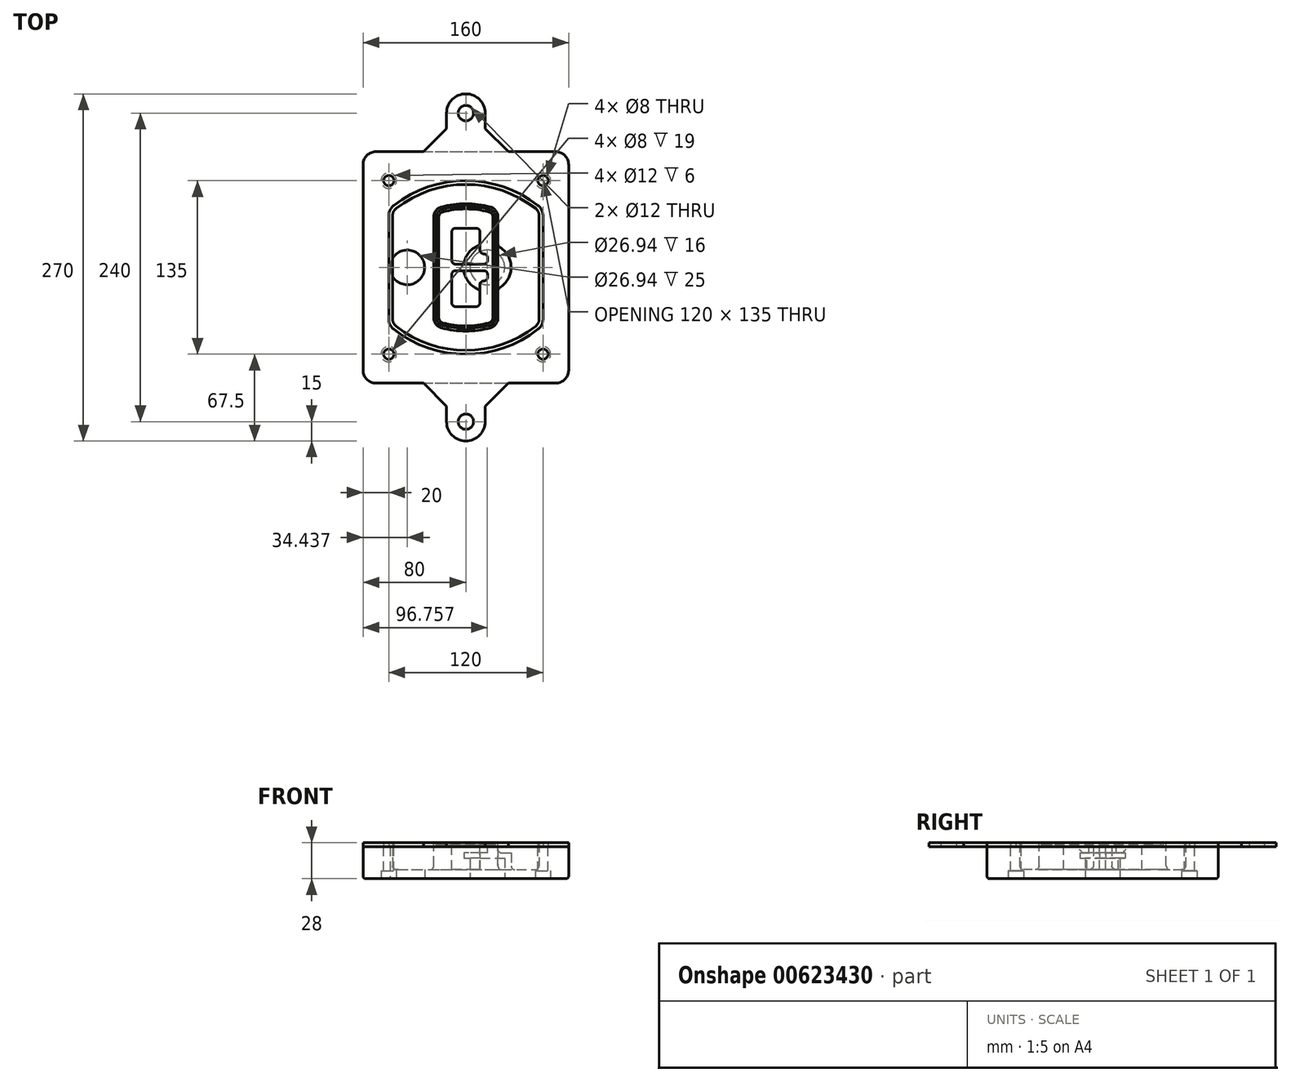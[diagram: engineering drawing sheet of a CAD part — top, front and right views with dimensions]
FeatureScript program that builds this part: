
annotation { "Feature Type Name" : "Feature", "Feature Type Description" : "" }
export const myFeature = defineFeature(function(context is Context, id is Id, definition is map)
    precondition{}
    {
        {
            var Q0;
            Q0=qCreatedBy(makeId("Top.planeOp"),FACE);
            var sketch = newSketch(context, id + "F0", { "sketchPlane" : qUnion([Q0])});
            skPoint(sketch, "E0.rect.middle", {"position": v(0, 0) * mm});
            skLineSegment(sketch, "E1.bottom", {"start": v(-70, -90) * mm, "end": v(70, -90) * mm});
            skLineSegment(sketch, "E1.top", {"start": v(-70, 90) * mm, "end": v(70, 90) * mm});
            skLineSegment(sketch, "E1.left", {"start": v(-80, -80) * mm, "end": v(-80, 80) * mm});
            skLineSegment(sketch, "E1.right", {"start": v(80, -80) * mm, "end": v(80, 80) * mm});
            skLineSegment(sketch, "E2", {"start": v(-80, 90) * mm, "end": v(80, -90) * mm, "construction": true});
            skLineSegment(sketch, "E3", {"start": v(80, 90) * mm, "end": v(-80, -90) * mm, "construction": true});
            skCircle(sketch, "E4", {"center": v(-60, 67.5) * mm, "radius": 4 * mm});
            skCircle(sketch, "E5", {"center": v(60, 67.5) * mm, "radius": 4 * mm});
            skCircle(sketch, "E6", {"center": v(60, -67.5) * mm, "radius": 4 * mm});
            skCircle(sketch, "E7", {"center": v(-60, -67.5) * mm, "radius": 4 * mm});
            skLineSegment(sketch, "E8", {"start": v(-60, 67.5) * mm, "end": v(60, 67.5) * mm, "construction": true});
            skLineSegment(sketch, "E9", {"start": v(60, 67.5) * mm, "end": v(60, -67.5) * mm, "construction": true});
            skLineSegment(sketch, "E10", {"start": v(60, -67.5) * mm, "end": v(-60, -67.5) * mm, "construction": true});
            skLineSegment(sketch, "E11", {"start": v(-60, -67.5) * mm, "end": v(-60, 67.5) * mm, "construction": true});
            skLineSegment(sketch, "E12", {"start": v(-60, 40.3) * mm, "end": v(-60, -40.3) * mm});
            skLineSegment(sketch, "E13", {"start": v(60, 40.3) * mm, "end": v(60, -40.3) * mm});
            skArc(sketch, "E14", {"start": v(56.15, 48.18) * mm, "mid": v(0, 67.5) * mm, "end": v(-56.15, 48.18) * mm});
            skArc(sketch, "E15", {"start": v(-56.15, -48.18) * mm, "mid": v(0, -67.5) * mm, "end": v(56.15, -48.18) * mm});
            skLineSegment(sketch, "E16", {"start": v(-60, 0) * mm, "end": v(60, 0) * mm, "construction": true});
            skPoint(sketch, "E17.visualSharp", {"position": v(-60, -45) * mm});
            skArc(sketch, "E17.filletArc", {"start": v(-60, -40.3) * mm, "mid": v(-58.99, -44.68) * mm, "end": v(-56.15, -48.18) * mm});
            skPoint(sketch, "E18.visualSharp", {"position": v(-60, 45) * mm});
            skArc(sketch, "E18.filletArc", {"start": v(-56.15, 48.18) * mm, "mid": v(-58.99, 44.68) * mm, "end": v(-60, 40.3) * mm});
            skPoint(sketch, "E19.visualSharp", {"position": v(60, 45) * mm});
            skArc(sketch, "E19.filletArc", {"start": v(60, 40.3) * mm, "mid": v(58.99, 44.68) * mm, "end": v(56.15, 48.18) * mm});
            skPoint(sketch, "E20.visualSharp", {"position": v(60, -45) * mm});
            skArc(sketch, "E20.filletArc", {"start": v(56.15, -48.18) * mm, "mid": v(58.99, -44.68) * mm, "end": v(60, -40.3) * mm});
            skPoint(sketch, "E21.visualSharp", {"position": v(-80, 90) * mm});
            skArc(sketch, "E21.filletArc", {"start": v(-70, 90) * mm, "mid": v(-77.07, 87.07) * mm, "end": v(-80, 80) * mm});
            skPoint(sketch, "E22.visualSharp", {"position": v(80, 90) * mm});
            skArc(sketch, "E22.filletArc", {"start": v(80, 80) * mm, "mid": v(77.07, 87.07) * mm, "end": v(70, 90) * mm});
            skPoint(sketch, "E23.visualSharp", {"position": v(80, -90) * mm});
            skArc(sketch, "E23.filletArc", {"start": v(70, -90) * mm, "mid": v(77.07, -87.07) * mm, "end": v(80, -80) * mm});
            skPoint(sketch, "E24.visualSharp", {"position": v(-80, -90) * mm});
            skArc(sketch, "E24.filletArc", {"start": v(-80, -80) * mm, "mid": v(-77.07, -87.07) * mm, "end": v(-70, -90) * mm});
            skArc(sketch, "E25.0", {"start": v(57, 40.3) * mm, "mid": v(56.3, 43.36) * mm, "end": v(54.3, 45.81) * mm});
            skLineSegment(sketch, "E25.1", {"start": v(57, 40.3) * mm, "end": v(57, -40.3) * mm});
            skArc(sketch, "E25.2", {"start": v(54.3, -45.81) * mm, "mid": v(56.3, -43.36) * mm, "end": v(57, -40.3) * mm});
            skArc(sketch, "E25.3", {"start": v(-54.3, -45.81) * mm, "mid": v(0, -64.5) * mm, "end": v(54.3, -45.81) * mm});
            skArc(sketch, "E25.4", {"start": v(-57, -40.3) * mm, "mid": v(-56.3, -43.36) * mm, "end": v(-54.3, -45.81) * mm});
            skArc(sketch, "E25.5", {"start": v(54.3, 45.81) * mm, "mid": v(0, 64.5) * mm, "end": v(-54.3, 45.81) * mm});
            skLineSegment(sketch, "E25.6", {"start": v(-57, 40.3) * mm, "end": v(-57, -40.3) * mm});
            skArc(sketch, "E25.7", {"start": v(-54.3, 45.81) * mm, "mid": v(-56.3, 43.36) * mm, "end": v(-57, 40.3) * mm});
            skArc(sketch, "E26.0", {"start": v(-58.62, 51.33) * mm, "mid": v(-62.58, 46.43) * mm, "end": v(-64, 40.3) * mm});
            skArc(sketch, "E26.1", {"start": v(58.62, 51.33) * mm, "mid": v(0, 71.5) * mm, "end": v(-58.62, 51.33) * mm});
            skArc(sketch, "E26.2", {"start": v(64, 40.3) * mm, "mid": v(62.58, 46.43) * mm, "end": v(58.62, 51.33) * mm});
            skLineSegment(sketch, "E26.3", {"start": v(64, 40.3) * mm, "end": v(64, -40.3) * mm});
            skArc(sketch, "E26.4", {"start": v(58.62, -51.33) * mm, "mid": v(62.58, -46.43) * mm, "end": v(64, -40.3) * mm});
            skLineSegment(sketch, "E26.5", {"start": v(-64, 40.3) * mm, "end": v(-64, -40.3) * mm});
            skArc(sketch, "E26.6", {"start": v(-58.62, -51.33) * mm, "mid": v(0, -71.5) * mm, "end": v(58.62, -51.33) * mm});
            skArc(sketch, "E26.7", {"start": v(-64, -40.3) * mm, "mid": v(-62.58, -46.43) * mm, "end": v(-58.62, -51.33) * mm});
            skSolve(sketch);
        }
        {
            var Q0;
            Q0=makeQuery(id+"F0.imprint","IMPRINT",FACE,{"disambiguationData":[TD([[makeQuery(id+"F0.imprint","IMPRINT",EDGE,{"derivedFrom":sQuery(id+"F0.wireOp",EDGE,"E1.bottom")}),1.0]])]});
            var Q1;
            Q1=makeQuery(id+"F0.imprint","IMPRINT",FACE,{"disambiguationData":[TD([[makeQuery(id+"F0.imprint","IMPRINT",EDGE,{"derivedFrom":sQuery(id+"F0.wireOp",EDGE,"E12")}),1.0]])]});
            var Q2;
            Q2=makeQuery(id+"F0.imprint","IMPRINT",FACE,{"disambiguationData":[TD([[makeQuery(id+"F0.imprint","IMPRINT",EDGE,{"derivedFrom":sQuery(id+"F0.wireOp",EDGE,"E25.0")}),1.0]])]});
            var Q3;
            Q3=makeQuery(id+"F0.imprint","IMPRINT",FACE,{"disambiguationData":[TD([[makeQuery(id+"F0.imprint","IMPRINT",EDGE,{"derivedFrom":sQuery(id+"F0.wireOp",EDGE,"E12")}),-1.0]])]});
            extrude(context, id + "F1", {"entities" : qUnion([Q0, Q1, Q2, Q3]), "oppositeDirection" : true, "depth" : 25 * mm});
        }
        {
            var Q0;
            Q0=makeQuery(id+"F0.imprint","IMPRINT",FACE,{"disambiguationData":[TD([[makeQuery(id+"F0.imprint","IMPRINT",EDGE,{"derivedFrom":sQuery(id+"F0.wireOp",EDGE,"E12")}),1.0]])]});
            extrude(context, id + "F2", {"entities" : qUnion([Q0]), "operationType" : NewBodyOperationType.ADD, "depth" : 3 * mm});
        }
        {
            var Q0;
            Q0=makeQuery(id+"F0.imprint","IMPRINT",FACE,{"disambiguationData":[TD([[makeQuery(id+"F0.imprint","IMPRINT",EDGE,{"derivedFrom":sQuery(id+"F0.wireOp",EDGE,"E25.0")}),1.0]])]});
            extrude(context, id + "F3", {"entities" : qUnion([Q0]), "operationType" : NewBodyOperationType.REMOVE, "oppositeDirection" : true, "depth" : 18 * mm});
        }
        {
            var Q0;
            Q0=makeQuery(id+"F2.opExtrude","CAP_FACE",FACE,{"disambiguationData":[OSD([sQuery(id+"F0.wireOp",EDGE,"E12"),sQuery(id+"F0.wireOp",EDGE,"E13"),sQuery(id+"F0.wireOp",EDGE,"E14"),sQuery(id+"F0.wireOp",EDGE,"E15"),sQuery(id+"F0.wireOp",EDGE,"E17.filletArc"),sQuery(id+"F0.wireOp",EDGE,"E18.filletArc"),sQuery(id+"F0.wireOp",EDGE,"E19.filletArc"),sQuery(id+"F0.wireOp",EDGE,"E20.filletArc"),sQuery(id+"F0.wireOp",EDGE,"E25.0"),sQuery(id+"F0.wireOp",EDGE,"E25.1"),sQuery(id+"F0.wireOp",EDGE,"E25.2"),sQuery(id+"F0.wireOp",EDGE,"E25.3"),sQuery(id+"F0.wireOp",EDGE,"E25.4"),sQuery(id+"F0.wireOp",EDGE,"E25.5"),sQuery(id+"F0.wireOp",EDGE,"E25.6"),sQuery(id+"F0.wireOp",EDGE,"E25.7")])],"isStart":false});
            var sketch = newSketch(context, id + "F4", { "sketchPlane" : qUnion([Q0])});
            skArc(sketch, "E27.0", {"start": v(-19.08, -46.97) * mm, "mid": v(0, -49.5) * mm, "end": v(19.08, -46.97) * mm});
            skArc(sketch, "E28.0", {"start": v(19.08, 46.97) * mm, "mid": v(0, 49.5) * mm, "end": v(-19.08, 46.97) * mm});
            skLineSegment(sketch, "E29", {"start": v(-25, 39.25) * mm, "end": v(-25, -39.25) * mm});
            skLineSegment(sketch, "E30", {"start": v(25, 39.25) * mm, "end": v(25, -39.25) * mm});
            skLineSegment(sketch, "E31", {"start": v(-25, 45.1) * mm, "end": v(25, 45.1) * mm, "construction": true});
            skLineSegment(sketch, "E32", {"start": v(-25, -45.1) * mm, "end": v(25, -45.1) * mm, "construction": true});
            skPoint(sketch, "E33.visualSharp", {"position": v(-25, 45.1) * mm});
            skArc(sketch, "E33.filletArc", {"start": v(-19.08, 46.97) * mm, "mid": v(-23.35, 44.11) * mm, "end": v(-25, 39.25) * mm});
            skPoint(sketch, "E34.visualSharp", {"position": v(25, 45.1) * mm});
            skArc(sketch, "E34.filletArc", {"start": v(25, 39.25) * mm, "mid": v(23.35, 44.11) * mm, "end": v(19.08, 46.97) * mm});
            skPoint(sketch, "E35.visualSharp", {"position": v(25, -45.1) * mm});
            skArc(sketch, "E35.filletArc", {"start": v(19.08, -46.97) * mm, "mid": v(23.35, -44.11) * mm, "end": v(25, -39.25) * mm});
            skPoint(sketch, "E36.visualSharp", {"position": v(-25, -45.1) * mm});
            skArc(sketch, "E36.filletArc", {"start": v(-25, -39.25) * mm, "mid": v(-23.35, -44.11) * mm, "end": v(-19.08, -46.97) * mm});
            skArc(sketch, "E37.0", {"start": v(54.3, 45.81) * mm, "mid": v(0, 64.5) * mm, "end": v(-54.3, 45.81) * mm});
            skArc(sketch, "E37.1", {"start": v(-54.3, 45.81) * mm, "mid": v(-56.3, 43.36) * mm, "end": v(-57, 40.3) * mm});
            skLineSegment(sketch, "E37.2", {"start": v(-57, 40.3) * mm, "end": v(-57, -40.3) * mm});
            skArc(sketch, "E37.3", {"start": v(-57, -40.3) * mm, "mid": v(-56.3, -43.36) * mm, "end": v(-54.3, -45.81) * mm});
            skArc(sketch, "E37.4", {"start": v(-54.3, -45.81) * mm, "mid": v(0, -64.5) * mm, "end": v(54.3, -45.81) * mm});
            skArc(sketch, "E37.5", {"start": v(54.3, -45.81) * mm, "mid": v(56.3, -43.36) * mm, "end": v(57, -40.3) * mm});
            skLineSegment(sketch, "E37.6", {"start": v(57, 40.3) * mm, "end": v(57, -40.3) * mm});
            skArc(sketch, "E37.7", {"start": v(57, 40.3) * mm, "mid": v(56.3, 43.36) * mm, "end": v(54.3, 45.81) * mm});
            skLineSegment(sketch, "E38.0", {"start": v(23, 39.25) * mm, "end": v(23, -39.25) * mm});
            skArc(sketch, "E38.1", {"start": v(18.56, -45.04) * mm, "mid": v(21.76, -42.9) * mm, "end": v(23, -39.25) * mm});
            skArc(sketch, "E38.2", {"start": v(-18.56, -45.04) * mm, "mid": v(0, -47.5) * mm, "end": v(18.56, -45.04) * mm});
            skArc(sketch, "E38.3", {"start": v(-23, -39.25) * mm, "mid": v(-21.76, -42.9) * mm, "end": v(-18.56, -45.04) * mm});
            skLineSegment(sketch, "E38.4", {"start": v(-23, 39.25) * mm, "end": v(-23, -39.25) * mm});
            skArc(sketch, "E38.5", {"start": v(23, 39.25) * mm, "mid": v(21.76, 42.9) * mm, "end": v(18.56, 45.04) * mm});
            skArc(sketch, "E38.6", {"start": v(-18.56, 45.04) * mm, "mid": v(-21.76, 42.9) * mm, "end": v(-23, 39.25) * mm});
            skArc(sketch, "E38.7", {"start": v(18.56, 45.04) * mm, "mid": v(0, 47.5) * mm, "end": v(-18.56, 45.04) * mm});
            skArc(sketch, "E39.0", {"start": v(21, 39.25) * mm, "mid": v(20.18, 41.68) * mm, "end": v(18.04, 43.1) * mm});
            skLineSegment(sketch, "E39.1", {"start": v(21, 39.25) * mm, "end": v(21, -39.25) * mm});
            skArc(sketch, "E39.2", {"start": v(18.04, -43.1) * mm, "mid": v(20.18, -41.68) * mm, "end": v(21, -39.25) * mm});
            skArc(sketch, "E39.3", {"start": v(-18.04, -43.1) * mm, "mid": v(0, -45.5) * mm, "end": v(18.04, -43.1) * mm});
            skArc(sketch, "E39.4", {"start": v(-21, -39.25) * mm, "mid": v(-20.18, -41.68) * mm, "end": v(-18.04, -43.1) * mm});
            skArc(sketch, "E39.5", {"start": v(18.04, 43.1) * mm, "mid": v(0, 45.5) * mm, "end": v(-18.04, 43.1) * mm});
            skLineSegment(sketch, "E39.6", {"start": v(-21, 39.25) * mm, "end": v(-21, -39.25) * mm});
            skArc(sketch, "E39.7", {"start": v(-18.04, 43.1) * mm, "mid": v(-20.18, 41.68) * mm, "end": v(-21, 39.25) * mm});
            skLineSegment(sketch, "E40", {"start": v(-25, 0) * mm, "end": v(25, 0) * mm, "construction": true});
            skLineSegment(sketch, "E41", {"start": v(-11, 5.5) * mm, "end": v(-11, 27.5) * mm});
            skLineSegment(sketch, "E42", {"start": v(-8, 30.5) * mm, "end": v(8, 30.5) * mm});
            skLineSegment(sketch, "E43", {"start": v(11, 27.5) * mm, "end": v(11, 13.5) * mm});
            skLineSegment(sketch, "E44", {"start": v(14, 10.5) * mm, "end": v(14, 10.5) * mm});
            skLineSegment(sketch, "E45", {"start": v(17, 7.5) * mm, "end": v(17, 5.5) * mm});
            skLineSegment(sketch, "E46", {"start": v(14, 2.5) * mm, "end": v(-8, 2.5) * mm});
            skPoint(sketch, "E47.visualSharp", {"position": v(-11, 30.5) * mm});
            skArc(sketch, "E47.filletArc", {"start": v(-8, 30.5) * mm, "mid": v(-10.12, 29.62) * mm, "end": v(-11, 27.5) * mm});
            skPoint(sketch, "E48.visualSharp", {"position": v(11, 30.5) * mm});
            skArc(sketch, "E48.filletArc", {"start": v(11, 27.5) * mm, "mid": v(10.12, 29.62) * mm, "end": v(8, 30.5) * mm});
            skPoint(sketch, "E49.visualSharp", {"position": v(11, 10.5) * mm});
            skArc(sketch, "E49.filletArc", {"start": v(11, 13.5) * mm, "mid": v(11.88, 11.38) * mm, "end": v(14, 10.5) * mm});
            skPoint(sketch, "E50.visualSharp", {"position": v(17, 10.5) * mm});
            skArc(sketch, "E50.filletArc", {"start": v(17, 7.5) * mm, "mid": v(16.12, 9.62) * mm, "end": v(14, 10.5) * mm});
            skPoint(sketch, "E51.visualSharp", {"position": v(17, 2.5) * mm});
            skArc(sketch, "E51.filletArc", {"start": v(14, 2.5) * mm, "mid": v(16.12, 3.38) * mm, "end": v(17, 5.5) * mm});
            skPoint(sketch, "E52.visualSharp", {"position": v(-11, 2.5) * mm});
            skArc(sketch, "E52.filletArc", {"start": v(-11, 5.5) * mm, "mid": v(-10.12, 3.38) * mm, "end": v(-8, 2.5) * mm});
            skLineSegment(sketch, "E53.0.MirrorCS", {"start": v(14, -2.5) * mm, "end": v(-8, -2.5) * mm});
            skArc(sketch, "E54.0.MirrorCS", {"start": v(-11, -5.5) * mm, "mid": v(-10.12, -3.38) * mm, "end": v(-8, -2.5) * mm});
            skLineSegment(sketch, "E55.0.MirrorCS", {"start": v(-11, -5.5) * mm, "end": v(-11, -27.5) * mm});
            skArc(sketch, "E56.0.MirrorCS", {"start": v(-8, -30.5) * mm, "mid": v(-10.12, -29.62) * mm, "end": v(-11, -27.5) * mm});
            skLineSegment(sketch, "E57.0.MirrorCS", {"start": v(-8, -30.5) * mm, "end": v(8, -30.5) * mm});
            skArc(sketch, "E58.0.MirrorCS", {"start": v(11, -27.5) * mm, "mid": v(10.12, -29.62) * mm, "end": v(8, -30.5) * mm});
            skLineSegment(sketch, "E59.0.MirrorCS", {"start": v(11, -27.5) * mm, "end": v(11, -13.5) * mm});
            skArc(sketch, "E60.0.MirrorCS", {"start": v(11, -13.5) * mm, "mid": v(11.88, -11.38) * mm, "end": v(14, -10.5) * mm});
            skArc(sketch, "E61.0.MirrorCS", {"start": v(17, -7.5) * mm, "mid": v(16.12, -9.62) * mm, "end": v(14, -10.5) * mm});
            skLineSegment(sketch, "E62.0.MirrorCS", {"start": v(17, -7.5) * mm, "end": v(17, -5.5) * mm});
            skArc(sketch, "E63.0.MirrorCS", {"start": v(14, -2.5) * mm, "mid": v(16.12, -3.38) * mm, "end": v(17, -5.5) * mm});
            skSolve(sketch);
        }
        {
            var Q0;
            Q0=makeQuery(id+"F4.imprint","IMPRINT",FACE,{"disambiguationData":[TD([[makeQuery(id+"F4.imprint","IMPRINT",EDGE,{"derivedFrom":sQuery(id+"F4.wireOp",EDGE,"E27.0")}),1.0]])]});
            var Q1;
            Q1=makeQuery(id+"F4.imprint","IMPRINT",FACE,{"disambiguationData":[TD([[makeQuery(id+"F4.imprint","IMPRINT",EDGE,{"derivedFrom":sQuery(id+"F4.wireOp",EDGE,"E38.0")}),-1.0]])]});
            var Q2;
            Q2=makeQuery(id+"F4.imprint","IMPRINT",FACE,{"disambiguationData":[TD([[makeQuery(id+"F4.imprint","IMPRINT",EDGE,{"derivedFrom":sQuery(id+"F4.wireOp",EDGE,"E39.0")}),1.0]])]});
            extrude(context, id + "F5", {"entities" : qUnion([Q0, Q1, Q2]), "operationType" : NewBodyOperationType.ADD, "endBound" : BoundingType.UP_TO_NEXT, "oppositeDirection" : true, "depth" : 25 * mm});
        }
        {
            var Q0;
            Q0=makeQuery(id+"F4.imprint","IMPRINT",FACE,{"disambiguationData":[TD([[makeQuery(id+"F4.imprint","IMPRINT",EDGE,{"derivedFrom":sQuery(id+"F4.wireOp",EDGE,"E38.0")}),-1.0]])]});
            extrude(context, id + "F6", {"entities" : qUnion([Q0]), "operationType" : NewBodyOperationType.REMOVE, "oppositeDirection" : true, "depth" : 2 * mm});
        }
        {
            var Q0;
            Q0=makeQuery(id+"F1.opExtrude","CAP_FACE",FACE,{"disambiguationData":[OSD([sQuery(id+"F0.wireOp",EDGE,"E1.bottom"),sQuery(id+"F0.wireOp",EDGE,"E1.top"),sQuery(id+"F0.wireOp",EDGE,"E1.left"),sQuery(id+"F0.wireOp",EDGE,"E1.right"),sQuery(id+"F0.wireOp",EDGE,"E4"),sQuery(id+"F0.wireOp",EDGE,"E5"),sQuery(id+"F0.wireOp",EDGE,"E6"),sQuery(id+"F0.wireOp",EDGE,"E7"),sQuery(id+"F0.wireOp",EDGE,"E21.filletArc"),sQuery(id+"F0.wireOp",EDGE,"E22.filletArc"),sQuery(id+"F0.wireOp",EDGE,"E23.filletArc"),sQuery(id+"F0.wireOp",EDGE,"E24.filletArc")])],"isStart":false});
            var sketch = newSketch(context, id + "F7", { "sketchPlane" : qUnion([Q0])});
            skCircle(sketch, "E64", {"center": v(16.76, 0) * mm, "radius": 13.47 * mm});
            skCircle(sketch, "E65", {"center": v(-45.56, 0) * mm, "radius": 13.47 * mm});
            skLineSegment(sketch, "E66", {"start": v(80, 0) * mm, "end": v(-80, 0) * mm});
            skCircle(sketch, "E67", {"center": v(16.76, 0) * mm, "radius": 18.47 * mm});
            skCircle(sketch, "E68", {"center": v(60, -67.5) * mm, "radius": 6 * mm});
            skCircle(sketch, "E69", {"center": v(-60, -67.5) * mm, "radius": 6 * mm});
            skCircle(sketch, "E70", {"center": v(-60, 67.5) * mm, "radius": 6 * mm});
            skCircle(sketch, "E71", {"center": v(60, 67.5) * mm, "radius": 6 * mm});
            skSolve(sketch);
        }
        {
            var Q0;
            {var subQ1=sQuery(id+"F7.wireOp",EDGE,"E66");var subQ4=sQuery(id+"F7.wireOp",EDGE,"E64");var subQ6=makeQuery(id+"F7.imprint","INTERSECT",VERTEX,{"disambiguationData":[OD(0.0)],"derivedFrom":[subQ4,subQ1]});Q0=makeQuery(id+"F7.imprint","IMPRINT",FACE,{"disambiguationData":[TD([[makeQuery(id+"F7.imprint","IMPRINT",EDGE,{"disambiguationData":[TD([[subQ6,-1.0]])],"derivedFrom":subQ4}),-1.0]])]});}
            var Q1;
            {var subQ0=sQuery(id+"F7.wireOp",EDGE,"E66");var subQ1=sQuery(id+"F7.wireOp",EDGE,"E64");var subQ3=makeQuery(id+"F7.imprint","INTERSECT",VERTEX,{"disambiguationData":[OD(0.0)],"derivedFrom":[subQ1,subQ0]});Q1=makeQuery(id+"F7.imprint","IMPRINT",FACE,{"disambiguationData":[TD([[makeQuery(id+"F7.imprint","IMPRINT",EDGE,{"disambiguationData":[TD([[subQ3,-1.0]])],"derivedFrom":subQ1}),1.0]])]});}
            var Q2;
            {var subQ0=sQuery(id+"F7.wireOp",EDGE,"E66");var subQ1=sQuery(id+"F7.wireOp",EDGE,"E64");var subQ3=makeQuery(id+"F7.imprint","INTERSECT",VERTEX,{"disambiguationData":[OD(0.0)],"derivedFrom":[subQ1,subQ0]});Q2=makeQuery(id+"F7.imprint","IMPRINT",FACE,{"disambiguationData":[TD([[makeQuery(id+"F7.imprint","IMPRINT",EDGE,{"disambiguationData":[TD([[subQ3,1.0]])],"derivedFrom":subQ1}),1.0]])]});}
            var Q3;
            {var subQ1=sQuery(id+"F7.wireOp",EDGE,"E66");var subQ4=sQuery(id+"F7.wireOp",EDGE,"E64");var subQ6=makeQuery(id+"F7.imprint","INTERSECT",VERTEX,{"disambiguationData":[OD(0.0)],"derivedFrom":[subQ4,subQ1]});Q3=makeQuery(id+"F7.imprint","IMPRINT",FACE,{"disambiguationData":[TD([[makeQuery(id+"F7.imprint","IMPRINT",EDGE,{"disambiguationData":[TD([[subQ6,1.0]])],"derivedFrom":subQ4}),-1.0]])]});}
            extrude(context, id + "F8", {"entities" : qUnion([Q0, Q1, Q2, Q3]), "operationType" : NewBodyOperationType.ADD, "oppositeDirection" : true, "depth" : 20 * mm});
        }
        {
            var Q0;
            {var subQ0=sQuery(id+"F7.wireOp",EDGE,"E66");var subQ1=sQuery(id+"F7.wireOp",EDGE,"E64");var subQ3=makeQuery(id+"F7.imprint","INTERSECT",VERTEX,{"disambiguationData":[OD(0.0)],"derivedFrom":[subQ1,subQ0]});Q0=makeQuery(id+"F7.imprint","IMPRINT",FACE,{"disambiguationData":[TD([[makeQuery(id+"F7.imprint","IMPRINT",EDGE,{"disambiguationData":[TD([[subQ3,-1.0]])],"derivedFrom":subQ1}),1.0]])]});}
            var Q1;
            {var subQ0=sQuery(id+"F7.wireOp",EDGE,"E66");var subQ1=sQuery(id+"F7.wireOp",EDGE,"E64");var subQ3=makeQuery(id+"F7.imprint","INTERSECT",VERTEX,{"disambiguationData":[OD(0.0)],"derivedFrom":[subQ1,subQ0]});Q1=makeQuery(id+"F7.imprint","IMPRINT",FACE,{"disambiguationData":[TD([[makeQuery(id+"F7.imprint","IMPRINT",EDGE,{"disambiguationData":[TD([[subQ3,1.0]])],"derivedFrom":subQ1}),1.0]])]});}
            extrude(context, id + "F9", {"entities" : qUnion([Q0, Q1]), "operationType" : NewBodyOperationType.REMOVE, "oppositeDirection" : true, "depth" : 16 * mm});
        }
        {
            var Q0;
            {var subQ0=sQuery(id+"F7.wireOp",EDGE,"E66");var subQ1=sQuery(id+"F7.wireOp",EDGE,"E65");var subQ3=makeQuery(id+"F7.imprint","INTERSECT",VERTEX,{"disambiguationData":[OD(0.0)],"derivedFrom":[subQ1,subQ0]});Q0=makeQuery(id+"F7.imprint","IMPRINT",FACE,{"disambiguationData":[TD([[makeQuery(id+"F7.imprint","IMPRINT",EDGE,{"disambiguationData":[TD([[subQ3,-1.0]])],"derivedFrom":subQ1}),1.0]])]});}
            var Q1;
            {var subQ0=sQuery(id+"F7.wireOp",EDGE,"E66");var subQ1=sQuery(id+"F7.wireOp",EDGE,"E65");var subQ3=makeQuery(id+"F7.imprint","INTERSECT",VERTEX,{"disambiguationData":[OD(0.0)],"derivedFrom":[subQ1,subQ0]});Q1=makeQuery(id+"F7.imprint","IMPRINT",FACE,{"disambiguationData":[TD([[makeQuery(id+"F7.imprint","IMPRINT",EDGE,{"disambiguationData":[TD([[subQ3,1.0]])],"derivedFrom":subQ1}),1.0]])]});}
            extrude(context, id + "F10", {"entities" : qUnion([Q0, Q1]), "operationType" : NewBodyOperationType.REMOVE, "oppositeDirection" : true, "depth" : 25 * mm});
        }
        {
            var Q0;
            Q0=makeQuery(id+"F7.imprint","IMPRINT",FACE,{"disambiguationData":[TD([[makeQuery(id+"F7.imprint","IMPRINT",EDGE,{"derivedFrom":sQuery(id+"F7.wireOp",EDGE,"E68")}),1.0]])]});
            var Q1;
            Q1=makeQuery(id+"F7.imprint","IMPRINT",FACE,{"disambiguationData":[TD([[makeQuery(id+"F7.imprint","IMPRINT",EDGE,{"derivedFrom":makeQuery(id+"F1.opExtrude","CAP_EDGE",EDGE,{"disambiguationData":[OSD([sQuery(id+"F0.wireOp",EDGE,"E5")])],"isStart":false})}),-1.0]])]});
            var Q2;
            Q2=makeQuery(id+"F7.imprint","IMPRINT",FACE,{"disambiguationData":[TD([[makeQuery(id+"F7.imprint","IMPRINT",EDGE,{"derivedFrom":sQuery(id+"F7.wireOp",EDGE,"E69")}),1.0]])]});
            var Q3;
            Q3=makeQuery(id+"F7.imprint","IMPRINT",FACE,{"disambiguationData":[TD([[makeQuery(id+"F7.imprint","IMPRINT",EDGE,{"derivedFrom":makeQuery(id+"F1.opExtrude","CAP_EDGE",EDGE,{"disambiguationData":[OSD([sQuery(id+"F0.wireOp",EDGE,"E4")])],"isStart":false})}),-1.0]])]});
            var Q4;
            Q4=makeQuery(id+"F7.imprint","IMPRINT",FACE,{"disambiguationData":[TD([[makeQuery(id+"F7.imprint","IMPRINT",EDGE,{"derivedFrom":sQuery(id+"F7.wireOp",EDGE,"E70")}),1.0]])]});
            var Q5;
            Q5=makeQuery(id+"F7.imprint","IMPRINT",FACE,{"disambiguationData":[TD([[makeQuery(id+"F7.imprint","IMPRINT",EDGE,{"derivedFrom":makeQuery(id+"F1.opExtrude","CAP_EDGE",EDGE,{"disambiguationData":[OSD([sQuery(id+"F0.wireOp",EDGE,"E7")])],"isStart":false})}),-1.0]])]});
            var Q6;
            Q6=makeQuery(id+"F7.imprint","IMPRINT",FACE,{"disambiguationData":[TD([[makeQuery(id+"F7.imprint","IMPRINT",EDGE,{"derivedFrom":sQuery(id+"F7.wireOp",EDGE,"E71")}),1.0]])]});
            var Q7;
            Q7=makeQuery(id+"F7.imprint","IMPRINT",FACE,{"disambiguationData":[TD([[makeQuery(id+"F7.imprint","IMPRINT",EDGE,{"derivedFrom":makeQuery(id+"F1.opExtrude","CAP_EDGE",EDGE,{"disambiguationData":[OSD([sQuery(id+"F0.wireOp",EDGE,"E6")])],"isStart":false})}),-1.0]])]});
            extrude(context, id + "F11", {"entities" : qUnion([Q0, Q1, Q2, Q3, Q4, Q5, Q6, Q7]), "operationType" : NewBodyOperationType.REMOVE, "oppositeDirection" : true, "depth" : 6 * mm});
        }
        {
            var Q0;
            Q0=makeQuery(id+"F9.boolean.opBoolean","COPY",FACE,{"derivedFrom":makeQuery(id+"F9.opExtrude","CAP_FACE",FACE,{"disambiguationData":[OSD([sQuery(id+"F7.wireOp",EDGE,"E64")])],"isStart":false})});
            var sketch = newSketch(context, id + "F12", { "sketchPlane" : qUnion([Q0])});
            skArc(sketch, "E72.0", {"start": v(11, 17.55) * mm, "mid": v(2.57, 11.82) * mm, "end": v(-1.54, 2.5) * mm});
            skArc(sketch, "E72.1", {"start": v(-1.54, -2.5) * mm, "mid": v(2.57, -11.82) * mm, "end": v(11, -17.55) * mm});
            skLineSegment(sketch, "E73", {"start": v(-1.54, -2.5) * mm, "end": v(14, -2.5) * mm});
            skLineSegment(sketch, "E74.0", {"start": v(14, 2.5) * mm, "end": v(-1.54, 2.5) * mm});
            skArc(sketch, "E74.1", {"start": v(14, 2.5) * mm, "mid": v(16.12, 3.38) * mm, "end": v(17, 5.5) * mm});
            skLineSegment(sketch, "E74.2", {"start": v(17, 7.5) * mm, "end": v(17, 5.5) * mm});
            skArc(sketch, "E74.3", {"start": v(17, 7.5) * mm, "mid": v(16.12, 9.62) * mm, "end": v(14, 10.5) * mm});
            skArc(sketch, "E74.4", {"start": v(11, 13.5) * mm, "mid": v(11.88, 11.38) * mm, "end": v(14, 10.5) * mm});
            skLineSegment(sketch, "E74.5", {"start": v(11, 17.55) * mm, "end": v(11, 13.5) * mm});
            skLineSegment(sketch, "E74.7", {"start": v(14, -2.5) * mm, "end": v(-1.54, -2.5) * mm});
            skArc(sketch, "E74.8", {"start": v(14, -2.5) * mm, "mid": v(16.12, -3.38) * mm, "end": v(17, -5.5) * mm});
            skLineSegment(sketch, "E74.9", {"start": v(17, -7.5) * mm, "end": v(17, -5.5) * mm});
            skArc(sketch, "E74.10", {"start": v(17, -7.5) * mm, "mid": v(16.12, -9.62) * mm, "end": v(14, -10.5) * mm});
            skArc(sketch, "E74.11", {"start": v(11, -13.5) * mm, "mid": v(11.88, -11.38) * mm, "end": v(14, -10.5) * mm});
            skLineSegment(sketch, "E74.12", {"start": v(11, -17.55) * mm, "end": v(11, -13.5) * mm});
            skPoint(sketch, "E75.orphan", {"position": v(11, -27.5) * mm});
            skPoint(sketch, "E76.orphan", {"position": v(-8, -2.5) * mm});
            skPoint(sketch, "E77.orphan", {"position": v(-8, 2.5) * mm});
            skPoint(sketch, "E78.orphan", {"position": v(11, 27.5) * mm});
            skSolve(sketch);
        }
        {
            var Q0;
            {var subQ7=sQuery(id+"F12.wireOp",EDGE,"E72.0");var subQ14=sQuery(id+"F12.wireOp",EDGE,"E72.1");var subQ16=sQuery(id+"F12.wireOp",EDGE,"E74.1");var subQ18=sQuery(id+"F12.wireOp",EDGE,"E74.8");Q0=qUnion([makeQuery(id+"F12.imprint","IMPRINT",FACE,{"disambiguationData":[TD([[makeQuery(id+"F12.imprint","IMPRINT",EDGE,{"derivedFrom":subQ7}),1.0]])]}),makeQuery(id+"F12.imprint","IMPRINT",FACE,{"disambiguationData":[TD([[makeQuery(id+"F12.imprint","IMPRINT",EDGE,{"derivedFrom":subQ14}),1.0]])]}),makeQuery(id+"F12.imprint","IMPRINT",FACE,{"disambiguationData":[TD([[makeQuery(id+"F12.imprint","IMPRINT",EDGE,{"derivedFrom":subQ16}),1.0]])]}),makeQuery(id+"F12.imprint","IMPRINT",FACE,{"disambiguationData":[TD([[makeQuery(id+"F12.imprint","IMPRINT",EDGE,{"derivedFrom":subQ18}),-1.0]])]})]);}
            var Q1;
            Q1=makeQuery(id+"F5.boolean.opBoolean","SPLIT",FACE,{"disambiguationData":[TD([makeQuery(id+"F5.opExtrude","SWEPT_FACE",FACE,{"disambiguationData":[OSD([sQuery(id+"F4.wireOp",EDGE,"E41")])]})])],"derivedFrom":makeQuery(id+"F3.boolean.opBoolean","COPY",FACE,{"derivedFrom":makeQuery(id+"F3.opExtrude","CAP_FACE",FACE,{"disambiguationData":[OSD([sQuery(id+"F0.wireOp",EDGE,"E25.0"),sQuery(id+"F0.wireOp",EDGE,"E25.1"),sQuery(id+"F0.wireOp",EDGE,"E25.2"),sQuery(id+"F0.wireOp",EDGE,"E25.3"),sQuery(id+"F0.wireOp",EDGE,"E25.4"),sQuery(id+"F0.wireOp",EDGE,"E25.5"),sQuery(id+"F0.wireOp",EDGE,"E25.6"),sQuery(id+"F0.wireOp",EDGE,"E25.7")])],"isStart":false})})});
            extrude(context, id + "F13", {"entities" : qUnion([Q0]), "operationType" : NewBodyOperationType.REMOVE, "endBound" : BoundingType.UP_TO_SURFACE, "endBoundEntityFace" : qUnion([Q1]), "depth" : 25 * mm});
        }
        {
            var Q0;
            Q0=makeQuery(id+"F3.boolean.opBoolean","COPY",EDGE,{"derivedFrom":makeQuery(id+"F3.opExtrude","CAP_EDGE",EDGE,{"disambiguationData":[OSD([sQuery(id+"F0.wireOp",EDGE,"E25.6")])],"isStart":false})});
            var Q1;
            Q1=makeQuery(id+"F8.boolean.opBoolean","INTERSECT",EDGE,{"derivedFrom":[makeQuery(id+"F5.opExtrude","SWEPT_FACE",FACE,{"disambiguationData":[OSD([sQuery(id+"F4.wireOp",EDGE,"E30")])]}),makeQuery(id+"F8.opExtrude","CAP_FACE",FACE,{"disambiguationData":[OSD([sQuery(id+"F7.wireOp",EDGE,"E67")])],"isStart":false})]});
            var Q2;
            Q2=makeQuery(id+"F8.boolean.opBoolean","INTERSECT",EDGE,{"disambiguationData":[OD(1.0)],"derivedFrom":[makeQuery(id+"F5.opExtrude","SWEPT_FACE",FACE,{"disambiguationData":[OSD([sQuery(id+"F4.wireOp",EDGE,"E30")])]}),makeQuery(id+"F8.opExtrude","SWEPT_FACE",FACE,{"disambiguationData":[OSD([sQuery(id+"F7.wireOp",EDGE,"E67")])]})]});
            var Q3;
            {var subQ0=sQuery(id+"F4.wireOp",EDGE,"E30");Q3=makeQuery(id+"F8.boolean.opBoolean","SPLIT",EDGE,{"disambiguationData":[TD([makeQuery(id+"F5.opExtrude","SWEPT_FACE",FACE,{"disambiguationData":[OSD([sQuery(id+"F4.wireOp",EDGE,"E35.filletArc")])]})])],"derivedFrom":makeQuery(id+"F5.opExtrude","CAP_EDGE",EDGE,{"disambiguationData":[OSD([subQ0])],"isStart":false})});}
            var Q4;
            {var subQ0=sQuery(id+"F0.wireOp",EDGE,"E25.7");var subQ1=sQuery(id+"F0.wireOp",EDGE,"E25.1");var subQ2=sQuery(id+"F0.wireOp",EDGE,"E25.6");var subQ3=sQuery(id+"F0.wireOp",EDGE,"E25.5");var subQ4=sQuery(id+"F0.wireOp",EDGE,"E25.4");var subQ5=sQuery(id+"F0.wireOp",EDGE,"E25.0");var subQ6=sQuery(id+"F0.wireOp",EDGE,"E25.2");var subQ7=sQuery(id+"F0.wireOp",EDGE,"E25.3");Q4=makeQuery(id+"F8.boolean.opBoolean","INTERSECT",EDGE,{"derivedFrom":[makeQuery(id+"F5.boolean.opBoolean","SPLIT",FACE,{"disambiguationData":[TD([makeQuery(id+"F2.opExtrude","SWEPT_FACE",FACE,{"disambiguationData":[OSD([subQ5])]})])],"derivedFrom":makeQuery(id+"F3.boolean.opBoolean","COPY",FACE,{"derivedFrom":makeQuery(id+"F3.opExtrude","CAP_FACE",FACE,{"disambiguationData":[OSD([subQ5,subQ1,subQ6,subQ7,subQ4,subQ3,subQ2,subQ0])],"isStart":false})})}),makeQuery(id+"F8.opExtrude","SWEPT_FACE",FACE,{"disambiguationData":[OSD([sQuery(id+"F7.wireOp",EDGE,"E67")])]})]});}
            var Q5;
            Q5=makeQuery(id+"F8.boolean.opBoolean","INTERSECT",EDGE,{"disambiguationData":[OD(0.0)],"derivedFrom":[makeQuery(id+"F5.opExtrude","SWEPT_FACE",FACE,{"disambiguationData":[OSD([sQuery(id+"F4.wireOp",EDGE,"E30")])]}),makeQuery(id+"F8.opExtrude","SWEPT_FACE",FACE,{"disambiguationData":[OSD([sQuery(id+"F7.wireOp",EDGE,"E67")])]})]});
            fillet(context, id + "F14", {"entities" : qUnion([Q0, Q1, Q2, Q3, Q4, Q5]), "radius" : 3 * mm, "tangentPropagation" : true, "allowEdgeOverflow" : false});
        }
        {
            var Q0;
            Q0=makeQuery(id+"F1.opExtrude","CAP_EDGE",EDGE,{"disambiguationData":[OSD([sQuery(id+"F0.wireOp",EDGE,"E1.bottom")])],"isStart":false});
            fillet(context, id + "F15", {"entities" : qUnion([Q0]), "radius" : 2 * mm, "tangentPropagation" : true, "allowEdgeOverflow" : false});
        }
        {
            var Q0;
            {var subQ0=sQuery(id+"F0.wireOp",EDGE,"E21.filletArc");var subQ1=sQuery(id+"F0.wireOp",EDGE,"E7");var subQ2=sQuery(id+"F0.wireOp",EDGE,"E6");var subQ3=sQuery(id+"F0.wireOp",EDGE,"E5");var subQ4=sQuery(id+"F0.wireOp",EDGE,"E4");var subQ5=sQuery(id+"F0.wireOp",EDGE,"E22.filletArc");var subQ6=sQuery(id+"F0.wireOp",EDGE,"E1.bottom");var subQ7=sQuery(id+"F0.wireOp",EDGE,"E1.right");var subQ8=sQuery(id+"F0.wireOp",EDGE,"E1.top");var subQ9=sQuery(id+"F0.wireOp",EDGE,"E1.left");var subQ10=sQuery(id+"F0.wireOp",EDGE,"E23.filletArc");var subQ11=sQuery(id+"F0.wireOp",EDGE,"E24.filletArc");Q0=makeQuery(id+"F2.boolean.opBoolean","SPLIT",FACE,{"disambiguationData":[TD([makeQuery(id+"F1.opExtrude","SWEPT_FACE",FACE,{"disambiguationData":[OSD([subQ6])]})])],"derivedFrom":makeQuery(id+"F1.opExtrude","CAP_FACE",FACE,{"disambiguationData":[OSD([subQ6,subQ8,subQ9,subQ7,subQ4,subQ3,subQ2,subQ1,subQ0,subQ5,subQ10,subQ11])],"isStart":true})});}
            var sketch = newSketch(context, id + "F16", { "sketchPlane" : qUnion([Q0])});
            skLineSegment(sketch, "E79.0", {"start": v(80, -80) * mm, "end": v(80, 80) * mm});
            skArc(sketch, "E79.1", {"start": v(80, 80) * mm, "mid": v(77.07, 87.07) * mm, "end": v(70, 90) * mm});
            skLineSegment(sketch, "E79.2", {"start": v(-70, 90) * mm, "end": v(70, 90) * mm});
            skArc(sketch, "E79.3", {"start": v(-70, 90) * mm, "mid": v(-77.07, 87.07) * mm, "end": v(-80, 80) * mm});
            skLineSegment(sketch, "E79.4", {"start": v(-80, -80) * mm, "end": v(-80, 80) * mm});
            skArc(sketch, "E79.5", {"start": v(-80, -80) * mm, "mid": v(-77.07, -87.07) * mm, "end": v(-70, -90) * mm});
            skLineSegment(sketch, "E79.6", {"start": v(-70, -90) * mm, "end": v(70, -90) * mm});
            skArc(sketch, "E79.7", {"start": v(70, -90) * mm, "mid": v(77.07, -87.07) * mm, "end": v(80, -80) * mm});
            skLineSegment(sketch, "E79.8", {"start": v(-60, 40.3) * mm, "end": v(-60, -40.3) * mm});
            skArc(sketch, "E79.9", {"start": v(-56.15, 48.18) * mm, "mid": v(-58.99, 44.68) * mm, "end": v(-60, 40.3) * mm});
            skArc(sketch, "E79.10", {"start": v(56.15, 48.18) * mm, "mid": v(0, 67.5) * mm, "end": v(-56.15, 48.18) * mm});
            skArc(sketch, "E79.11", {"start": v(60, 40.3) * mm, "mid": v(58.99, 44.68) * mm, "end": v(56.15, 48.18) * mm});
            skLineSegment(sketch, "E79.12", {"start": v(60, 40.3) * mm, "end": v(60, -40.3) * mm});
            skArc(sketch, "E79.13", {"start": v(56.15, -48.18) * mm, "mid": v(58.99, -44.68) * mm, "end": v(60, -40.3) * mm});
            skArc(sketch, "E79.14", {"start": v(-56.15, -48.18) * mm, "mid": v(0, -67.5) * mm, "end": v(56.15, -48.18) * mm});
            skArc(sketch, "E79.15", {"start": v(-60, -40.3) * mm, "mid": v(-58.99, -44.68) * mm, "end": v(-56.15, -48.18) * mm});
            skCircle(sketch, "E80.16", {"center": v(-60, 67.5) * mm, "radius": 4 * mm});
            skCircle(sketch, "E80.17", {"center": v(60, 67.5) * mm, "radius": 4 * mm});
            skCircle(sketch, "E80.18", {"center": v(60, -67.5) * mm, "radius": 4 * mm});
            skCircle(sketch, "E80.19", {"center": v(-60, -67.5) * mm, "radius": 4 * mm});
            skLineSegment(sketch, "E81", {"start": v(0, 90) * mm, "end": v(0, 120) * mm, "construction": true});
            skPoint(sketch, "E81.endSnap0", {"position": v(0, 90) * mm});
            skCircle(sketch, "E82", {"center": v(0, 120) * mm, "radius": 6 * mm});
            skArc(sketch, "E83", {"start": v(15, 120) * mm, "mid": v(0, 135) * mm, "end": v(-15, 120) * mm});
            skLineSegment(sketch, "E84", {"start": v(-15, 120) * mm, "end": v(-15, 108) * mm});
            skLineSegment(sketch, "E85", {"start": v(-15, 108) * mm, "end": v(-33, 90) * mm});
            skLineSegment(sketch, "E86.MirrorCS", {"start": v(15, 120) * mm, "end": v(15, 108) * mm});
            skLineSegment(sketch, "E87.MirrorCS", {"start": v(15, 108) * mm, "end": v(33, 90) * mm});
            skLineSegment(sketch, "E88", {"start": v(-80, 0) * mm, "end": v(80, 0) * mm, "construction": true});
            skLineSegment(sketch, "E89.MirrorCS", {"start": v(15, -120) * mm, "end": v(15, -108) * mm});
            skLineSegment(sketch, "E90.MirrorCS", {"start": v(-15, -120) * mm, "end": v(-15, -108) * mm});
            skCircle(sketch, "E91.MirrorC", {"center": v(0, -120) * mm, "radius": 6 * mm});
            skLineSegment(sketch, "E92.MirrorCS", {"start": v(15, -108) * mm, "end": v(33, -90) * mm});
            skLineSegment(sketch, "E93.MirrorCS", {"start": v(0, -90) * mm, "end": v(0, -120) * mm, "construction": true});
            skLineSegment(sketch, "E94.MirrorCS", {"start": v(-15, -108) * mm, "end": v(-33, -90) * mm});
            skArc(sketch, "E95.MirrorCS", {"start": v(15, -120) * mm, "mid": v(0, -135) * mm, "end": v(-15, -120) * mm});
            skSolve(sketch);
        }
        {
            var Q0;
            Q0=makeQuery(id+"F16.imprint","IMPRINT",FACE,{"disambiguationData":[TD([[makeQuery(id+"F16.imprint","IMPRINT",EDGE,{"derivedFrom":sQuery(id+"F16.wireOp",EDGE,"E82")}),-1.0]])]});
            var Q1;
            Q1=makeQuery(id+"F16.imprint","IMPRINT",FACE,{"disambiguationData":[TD([[makeQuery(id+"F16.imprint","IMPRINT",EDGE,{"derivedFrom":sQuery(id+"F16.wireOp",EDGE,"E79.4")}),-1.0]])]});
            var Q2;
            Q2=makeQuery(id+"F16.imprint","IMPRINT",FACE,{"disambiguationData":[TD([[makeQuery(id+"F16.imprint","IMPRINT",EDGE,{"derivedFrom":sQuery(id+"F16.wireOp",EDGE,"E89.MirrorCS")}),1.0]])]});
            var Q3;
            Q3=makeQuery(id+"F2.opExtrude","CAP_FACE",FACE,{"disambiguationData":[OSD([sQuery(id+"F0.wireOp",EDGE,"E12"),sQuery(id+"F0.wireOp",EDGE,"E13"),sQuery(id+"F0.wireOp",EDGE,"E14"),sQuery(id+"F0.wireOp",EDGE,"E15"),sQuery(id+"F0.wireOp",EDGE,"E17.filletArc"),sQuery(id+"F0.wireOp",EDGE,"E18.filletArc"),sQuery(id+"F0.wireOp",EDGE,"E19.filletArc"),sQuery(id+"F0.wireOp",EDGE,"E20.filletArc"),sQuery(id+"F0.wireOp",EDGE,"E25.0"),sQuery(id+"F0.wireOp",EDGE,"E25.1"),sQuery(id+"F0.wireOp",EDGE,"E25.2"),sQuery(id+"F0.wireOp",EDGE,"E25.3"),sQuery(id+"F0.wireOp",EDGE,"E25.4"),sQuery(id+"F0.wireOp",EDGE,"E25.5"),sQuery(id+"F0.wireOp",EDGE,"E25.6"),sQuery(id+"F0.wireOp",EDGE,"E25.7")])],"isStart":false});
            extrude(context, id + "F17", {"entities" : qUnion([Q0, Q1, Q2]), "endBound" : BoundingType.UP_TO_SURFACE, "depth" : 25 * mm, "endBoundEntityFace" : qUnion([Q3]), "offsetDistance" : 25 * mm});
        }
    });
